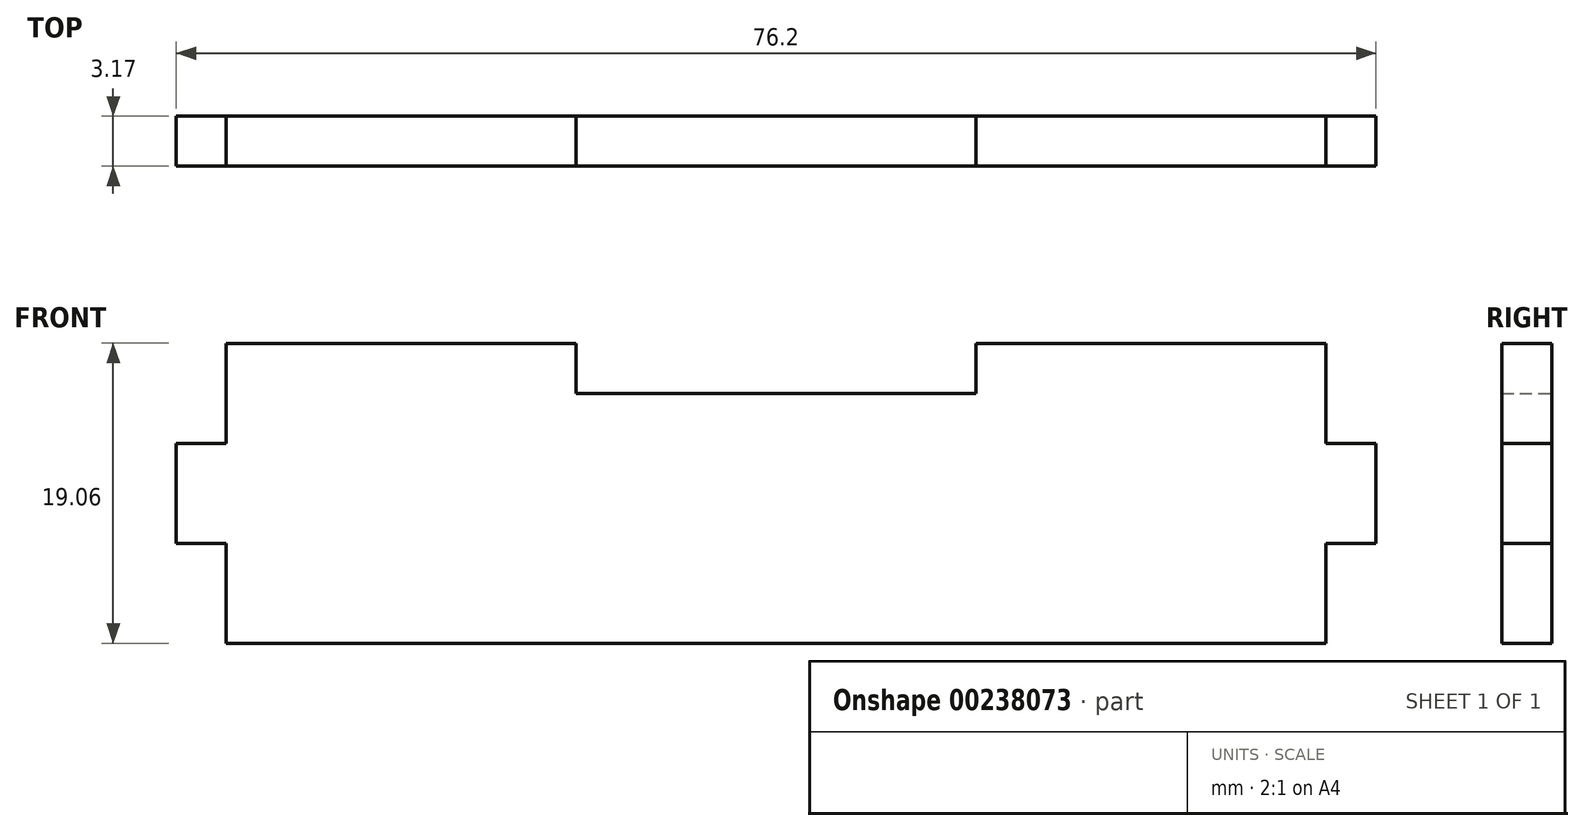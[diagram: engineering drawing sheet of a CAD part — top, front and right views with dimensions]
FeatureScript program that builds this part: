
annotation { "Feature Type Name" : "Feature", "Feature Type Description" : "" }
export const myFeature = defineFeature(function(context is Context, id is Id, definition is map)
    precondition{}
    {
        {
            var Q0;
            Q0=qCreatedBy(makeId("Front.planeOp"),FACE);
            var sketch = newSketch(context, id + "F0", { "sketchPlane" : qUnion([Q0])});
            skLineSegment(sketch, "E0.bottom", {"start": v(34.93, -9.52) * mm, "end": v(-34.93, -9.53) * mm});
            skLineSegment(sketch, "E0.top", {"start": v(34.93, 9.53) * mm, "end": v(-34.93, 9.53) * mm});
            skLineSegment(sketch, "E0.left", {"start": v(34.93, -9.52) * mm, "end": v(34.93, 9.53) * mm});
            skLineSegment(sketch, "E0.right", {"start": v(-34.93, -9.53) * mm, "end": v(-34.93, 9.52) * mm});
            skPoint(sketch, "E0.middle", {"position": v(0, 0) * mm});
            skLineSegment(sketch, "E1.bottom", {"start": v(-12.7, 9.52) * mm, "end": v(12.7, 9.53) * mm});
            skLineSegment(sketch, "E1.top", {"start": v(-12.7, 6.35) * mm, "end": v(12.7, 6.35) * mm});
            skLineSegment(sketch, "E1.left", {"start": v(-12.7, 9.52) * mm, "end": v(-12.7, 6.35) * mm});
            skLineSegment(sketch, "E1.right", {"start": v(12.7, 9.53) * mm, "end": v(12.7, 6.35) * mm});
            skLineSegment(sketch, "E2.bottom", {"start": v(-38.1, 3.17) * mm, "end": v(-34.93, 3.17) * mm});
            skLineSegment(sketch, "E2.top", {"start": v(-38.1, -3.18) * mm, "end": v(-34.93, -3.18) * mm});
            skLineSegment(sketch, "E2.left", {"start": v(-38.1, 3.17) * mm, "end": v(-38.1, -3.18) * mm});
            skLineSegment(sketch, "E2.right", {"start": v(-34.93, 3.17) * mm, "end": v(-34.93, -3.18) * mm});
            skLineSegment(sketch, "E3.bottom", {"start": v(34.92, 3.18) * mm, "end": v(38.1, 3.18) * mm});
            skLineSegment(sketch, "E3.top", {"start": v(34.92, -3.17) * mm, "end": v(38.1, -3.17) * mm});
            skLineSegment(sketch, "E3.left", {"start": v(34.93, 3.18) * mm, "end": v(34.93, -3.17) * mm});
            skLineSegment(sketch, "E3.right", {"start": v(38.1, 3.18) * mm, "end": v(38.1, -3.17) * mm});
            skSolve(sketch);
        }
        {
            var Q0;
            {var subQ4=sQuery(id+"F0.wireOp",EDGE,"E0.bottom");Q0=makeQuery(id+"F0.imprint","IMPRINT",FACE,{"disambiguationData":[TD([[makeQuery(id+"F0.imprint","IMPRINT",EDGE,{"derivedFrom":subQ4}),-1.0]])]});}
            var Q1;
            Q1=makeQuery(id+"F0.imprint","IMPRINT",FACE,{"disambiguationData":[TD([[makeQuery(id+"F0.imprint","IMPRINT",EDGE,{"derivedFrom":sQuery(id+"F0.wireOp",EDGE,"E2.bottom")}),-1.0]])]});
            var Q2;
            Q2=makeQuery(id+"F0.imprint","IMPRINT",FACE,{"disambiguationData":[TD([[makeQuery(id+"F0.imprint","IMPRINT",EDGE,{"derivedFrom":sQuery(id+"F0.wireOp",EDGE,"E3.bottom")}),-1.0]])]});
            extrude(context, id + "F1", {"entities" : qUnion([Q0, Q1, Q2]), "depth" : 3.17 * mm});
        }
    });
